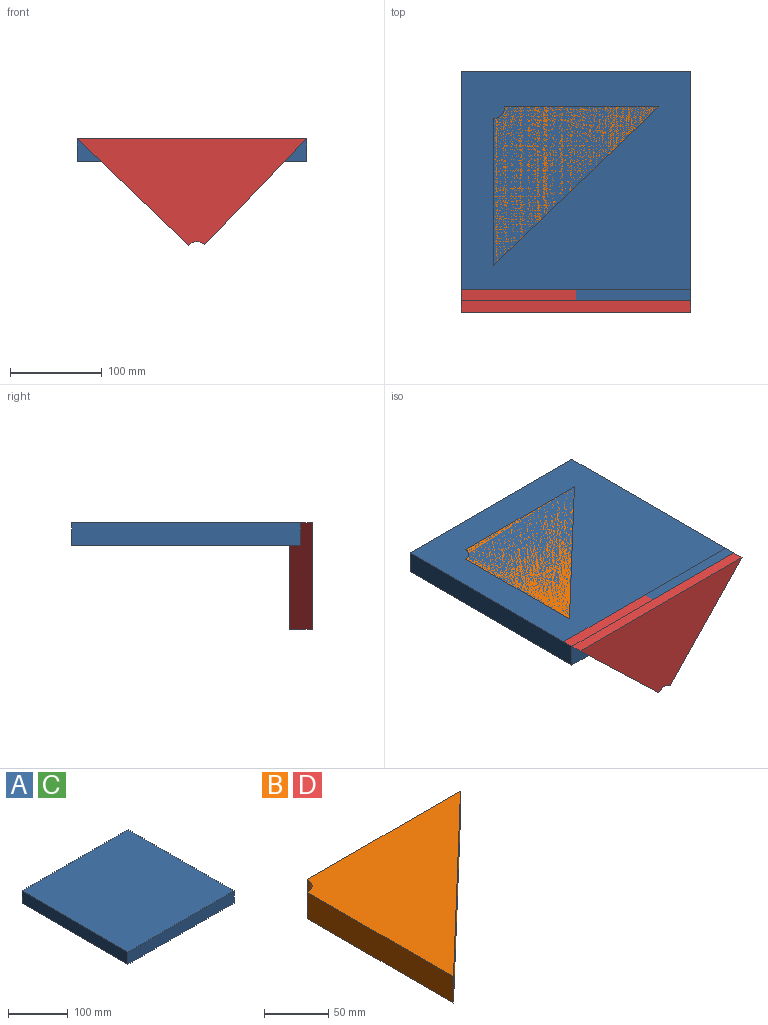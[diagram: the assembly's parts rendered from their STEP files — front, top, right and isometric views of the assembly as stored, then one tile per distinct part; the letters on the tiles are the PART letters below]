
ASSEMBLY  parts=4 mates=1
PART A: 6 faces, bbox 250x250x25 mm
  f0: plane 250x25mm, normal (0,-1,0), area 6250mm2, adj f1,f3,f4,f5
  f1: plane 250x25mm, normal (1,0,0), area 6250mm2, adj f0,f2,f4,f5
  f2: plane 250x25mm, normal (0,1,0), area 6250mm2, adj f1,f3,f4,f5
  f3: plane 250x25mm, normal (-1,0,0), area 6250mm2, adj f0,f2,f4,f5
  f4: plane 250x250mm, normal (0,0,1), area 62500mm2, adj f0,f1,f2,f3
  f5: plane 250x250mm, normal (0,0,-1), area 62500mm2, adj f0,f1,f2,f3
PART B: 6 faces, bbox 180.6x172.9x25 mm
  f0: plane 180.59x172.88mm, normal (0.69,-0.72,0), area 6250mm2, adj f1,f2,f3,f4
  f1: plane 168.09x25mm, normal (0,1,0), area 4202.1mm2, adj f0,f3,f4,f5
  f2: plane 160.38x25mm, normal (-1,0,0), area 4009.6mm2, adj f0,f3,f4,f5
  f3: plane 180.59x172.88mm, normal (0,0,1), area 15487.5mm2, adj f0,f1,f2,f5
  f4: plane 180.59x172.88mm, normal (0,0,-1), area 15487.5mm2, adj f0,f1,f2,f5
  f5: cylinder r=12.5mm len=25mm, axis (0,0,1), area 490.9mm2, adj f1,f2,f3,f4
PART C: same geometry as A
PART D: same geometry as B
PLACE A at identity
PLACE B at identity
PLACE C at identity
PLACE D rot(axis=(0.27,-0.68,0.68),149.4deg) t=(0,-112.5,25)mm
MATE parallel D.f0 <-> C.f4  axis (0,0,1) through (0,-125,25)mm
